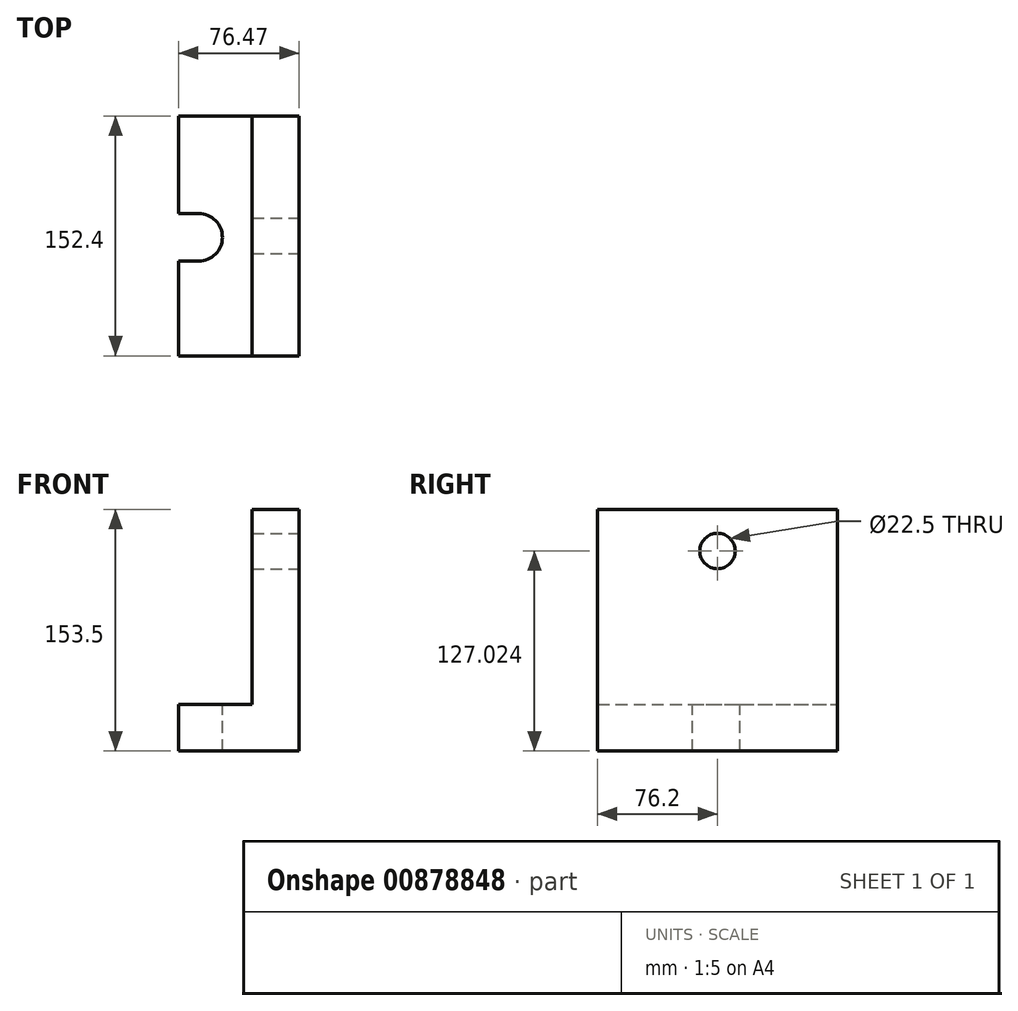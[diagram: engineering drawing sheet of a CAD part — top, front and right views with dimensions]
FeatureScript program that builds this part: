
annotation { "Feature Type Name" : "Feature", "Feature Type Description" : "" }
export const myFeature = defineFeature(function(context is Context, id is Id, definition is map)
    precondition{}
    {
        {
            var Q0;
            Q0=qCreatedBy(makeId("Front.planeOp"),FACE);
            var sketch = newSketch(context, id + "F0", { "sketchPlane" : qUnion([Q0])});
            skLineSegment(sketch, "E0", {"start": v(0, 0) * mm, "end": v(0, 153.5) * mm});
            skLineSegment(sketch, "E1", {"start": v(0, 153.5) * mm, "end": v(-29.7, 153.5) * mm});
            skLineSegment(sketch, "E2", {"start": v(-29.7, 153.5) * mm, "end": v(-29.7, 29.7) * mm});
            skLineSegment(sketch, "E3", {"start": v(0, 0) * mm, "end": v(-76.47, 0) * mm});
            skLineSegment(sketch, "E4", {"start": v(-76.47, 0) * mm, "end": v(-76.47, 29.7) * mm});
            skLineSegment(sketch, "E5", {"start": v(-76.47, 29.7) * mm, "end": v(-29.7, 29.7) * mm});
            skSolve(sketch);
        }
        {
            var Q0;
            Q0=makeQuery(id+"F0.imprint","IMPRINT",FACE,{"disambiguationData":[TD([[makeQuery(id+"F0.imprint","IMPRINT",EDGE,{"derivedFrom":sQuery(id+"F0.wireOp",EDGE,"E0")}),1.0]])]});
            extrude(context, id + "F1", {"entities" : qUnion([Q0]), "endBound" : BoundingType.SYMMETRIC, "depth" : 152.4 * mm, "offsetDistance" : 25.4 * mm});
        }
        {
            var Q0;
            Q0=makeQuery(id+"F1.opExtrude","SWEPT_FACE",FACE,{"disambiguationData":[OSD([sQuery(id+"F0.wireOp",EDGE,"E0")])]});
            var sketch = newSketch(context, id + "F2", { "sketchPlane" : qUnion([Q0])});
            skCircle(sketch, "E6", {"center": v(0, 127.02) * mm, "radius": 11.25 * mm});
            skSolve(sketch);
        }
        {
            var Q0;
            Q0=makeQuery(id+"F2.imprint","IMPRINT",FACE,{"disambiguationData":[TD([[makeQuery(id+"F2.imprint","IMPRINT",EDGE,{"derivedFrom":sQuery(id+"F2.wireOp",EDGE,"E6")}),1.0]])]});
            extrude(context, id + "F3", {"entities" : qUnion([Q0]), "operationType" : NewBodyOperationType.REMOVE, "endBound" : BoundingType.THROUGH_ALL, "oppositeDirection" : true, "depth" : 25.4 * mm, "offsetDistance" : 25.4 * mm});
        }
        {
            var Q0;
            Q0=makeQuery(id+"F1.opExtrude","SWEPT_FACE",FACE,{"disambiguationData":[OSD([sQuery(id+"F0.wireOp",EDGE,"E5")])]});
            var sketch = newSketch(context, id + "F4", { "sketchPlane" : qUnion([Q0])});
            skLineSegment(sketch, "E7", {"start": v(-63.77, 0) * mm, "end": v(-63.77, -0.94) * mm});
            skLineSegment(sketch, "E8", {"start": v(-63.77, -16.07) * mm, "end": v(-76.47, -16.07) * mm});
            skLineSegment(sketch, "E9", {"start": v(-76.47, -16.07) * mm, "end": v(-76.47, 14.2) * mm});
            skLineSegment(sketch, "E10", {"start": v(-76.47, 14.2) * mm, "end": v(-63.77, 14.2) * mm});
            skPoint(sketch, "E11.start.orphan", {"position": v(-76.47, 0) * mm});
            skArc(sketch, "E12", {"start": v(-63.77, -16.07) * mm, "mid": v(-48.64, -0.94) * mm, "end": v(-63.77, 14.2) * mm});
            skSolve(sketch);
        }
        {
            var Q0;
            Q0=makeQuery(id+"F4.imprint","IMPRINT",FACE,{"disambiguationData":[TD([[makeQuery(id+"F4.imprint","IMPRINT",EDGE,{"derivedFrom":sQuery(id+"F4.wireOp",EDGE,"E8")}),-1.0]])]});
            extrude(context, id + "F5", {"entities" : qUnion([Q0]), "operationType" : NewBodyOperationType.REMOVE, "endBound" : BoundingType.THROUGH_ALL, "oppositeDirection" : true, "depth" : 25.4 * mm, "offsetDistance" : 25.4 * mm});
        }
    });
